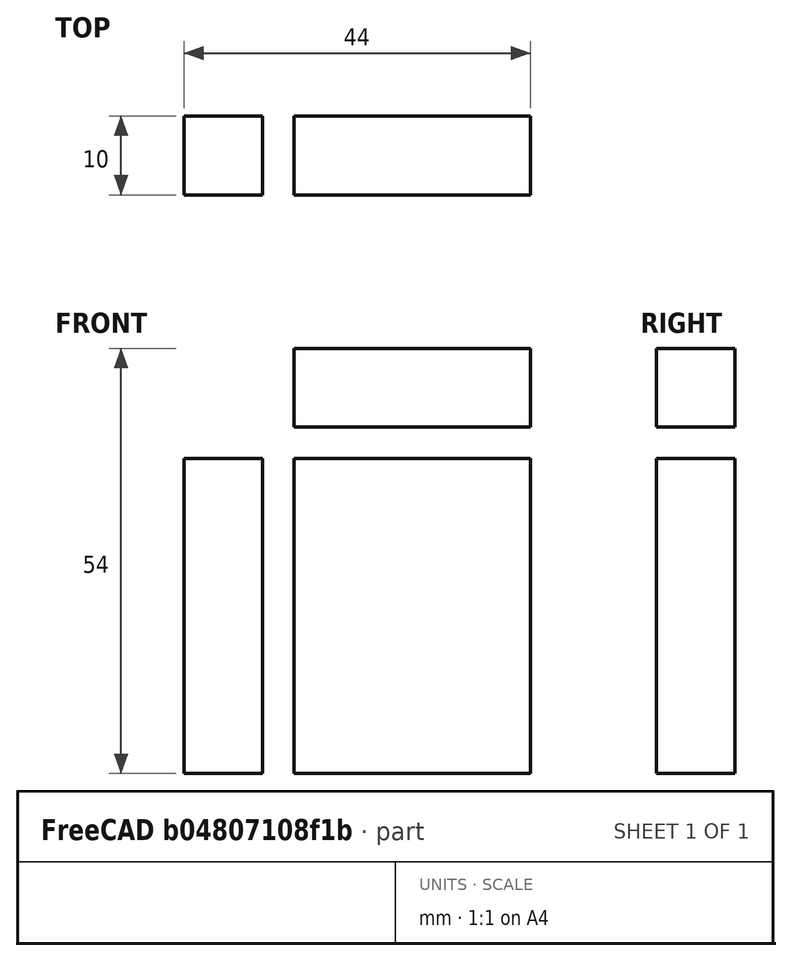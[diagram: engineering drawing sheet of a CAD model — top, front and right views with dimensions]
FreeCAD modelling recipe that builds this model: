
FCSTD DOCUMENT  (FreeCAD 0.17R13509 (Git))
Label: mode1_tns_mode2
License: All rights reserved
LicenseURL: http://en.wikipedia.org/wiki/All_rights_reserved
objects: Part::Box×19, Part::MultiFuse×7
note: 26 computed .brp shape members not serialized (recipe doc carries the construction recipe); baked Part::Feature solids carry a one-line shape summary decoded from their .brp

FEATURE [Part::Box] Box004  label="Cube004"
  AttacherType = Attacher::AttachEngine3D
  Height = 10
  Length = 10
  Placement = pos=(14,0,0) rot=(0,0,1;0rad)
  Width = 10
FEATURE [Part::Box] Box006  label="Cube006"
  AttacherType = Attacher::AttachEngine3D
  Height = 10
  Length = 10
  Placement = pos=(14,0,20) rot=(0,0,1;0rad)
  Width = 10
FEATURE [Part::Box] Box003  label="Cube003"
  AttacherType = Attacher::AttachEngine3D
  Height = 10
  Length = 10
  Placement = pos=(0,0,30) rot=(0,0,1;0rad)
  Width = 10
FEATURE [Part::Box] Box  label="Cube"
  AttacherType = Attacher::AttachEngine3D
  Height = 10
  Length = 10
  Width = 10
FEATURE [Part::Box] Box001  label="Cube001"
  AttacherType = Attacher::AttachEngine3D
  Height = 10
  Length = 10
  Placement = pos=(0,0,10) rot=(0,0,1;0rad)
  Width = 10
FEATURE [Part::Box] Box002  label="Cube002"
  AttacherType = Attacher::AttachEngine3D
  Height = 10
  Length = 10
  Placement = pos=(0,0,20) rot=(0,0,1;0rad)
  Width = 10
FEATURE [Part::MultiFuse] Fusion  label="Mode 1"
  Shapes = -> [Box,Box003,Box001,Box002]
FEATURE [Part::Box] Box005  label="Cube005"
  AttacherType = Attacher::AttachEngine3D
  Height = 10
  Length = 10
  Placement = pos=(14,0,10) rot=(0,0,1;0rad)
  Width = 10
FEATURE [Part::MultiFuse] Fusion001  label="Mode 2"
  Placement = pos=(14,0,68) rot=(0,1,0;1.5708rad)
  Shapes = -> [Box004,Box006,Box005]
FEATURE [Part::Box] Box007  label="Cube007"
  AttacherType = Attacher::AttachEngine3D
  Height = 10
  Length = 10
  Placement = pos=(14,0,30) rot=(0,0,1;0rad)
  Width = 10
FEATURE [Part::Box] Box008  label="Cube008"
  AttacherType = Attacher::AttachEngine3D
  Height = 10
  Length = 10
  Placement = pos=(24,0,30) rot=(0,0,1;0rad)
  Width = 10
FEATURE [Part::Box] Box009  label="Cube009"
  AttacherType = Attacher::AttachEngine3D
  Height = 10
  Length = 10
  Placement = pos=(34,0,30) rot=(0,0,1;0rad)
  Width = 10
FEATURE [Part::MultiFuse] Fusion002
  Shapes = -> [Box007,Box008,Box009]
FEATURE [Part::Box] Box010  label="Cube010"
  AttacherType = Attacher::AttachEngine3D
  Height = 10
  Length = 10
  Placement = pos=(14,0,30) rot=(0,0,1;0rad)
  Width = 10
FEATURE [Part::Box] Box011  label="Cube011"
  AttacherType = Attacher::AttachEngine3D
  Height = 10
  Length = 10
  Placement = pos=(34,0,30) rot=(0,0,1;0rad)
  Width = 10
FEATURE [Part::Box] Box012  label="Cube012"
  AttacherType = Attacher::AttachEngine3D
  Height = 10
  Length = 10
  Placement = pos=(24,0,30) rot=(0,0,1;0rad)
  Width = 10
FEATURE [Part::MultiFuse] Fusion003
  Placement = pos=(0,0,-10) rot=(0,0,1;0rad)
  Shapes = -> [Box010,Box012,Box011]
FEATURE [Part::Box] Box013  label="Cube013"
  AttacherType = Attacher::AttachEngine3D
  Height = 10
  Length = 10
  Placement = pos=(14,0,30) rot=(0,0,1;0rad)
  Width = 10
FEATURE [Part::Box] Box014  label="Cube014"
  AttacherType = Attacher::AttachEngine3D
  Height = 10
  Length = 10
  Placement = pos=(34,0,30) rot=(0,0,1;0rad)
  Width = 10
FEATURE [Part::Box] Box015  label="Cube015"
  AttacherType = Attacher::AttachEngine3D
  Height = 10
  Length = 10
  Placement = pos=(24,0,30) rot=(0,0,1;0rad)
  Width = 10
FEATURE [Part::MultiFuse] Fusion004
  Placement = pos=(0,0,-20) rot=(0,0,1;0rad)
  Shapes = -> [Box013,Box015,Box014]
FEATURE [Part::Box] Box016  label="Cube016"
  AttacherType = Attacher::AttachEngine3D
  Height = 10
  Length = 10
  Placement = pos=(14,0,30) rot=(0,0,1;0rad)
  Width = 10
FEATURE [Part::Box] Box017  label="Cube017"
  AttacherType = Attacher::AttachEngine3D
  Height = 10
  Length = 10
  Placement = pos=(34,0,30) rot=(0,0,1;0rad)
  Width = 10
FEATURE [Part::Box] Box018  label="Cube018"
  AttacherType = Attacher::AttachEngine3D
  Height = 10
  Length = 10
  Placement = pos=(24,0,30) rot=(0,0,1;0rad)
  Width = 10
FEATURE [Part::MultiFuse] Fusion005
  Placement = pos=(0,0,-30) rot=(0,0,1;0rad)
  Shapes = -> [Box016,Box018,Box017]
FEATURE [Part::MultiFuse] Fusion006  label="Mode12"
  Shapes = -> [Fusion002,Fusion003,Fusion005,Fusion004]
